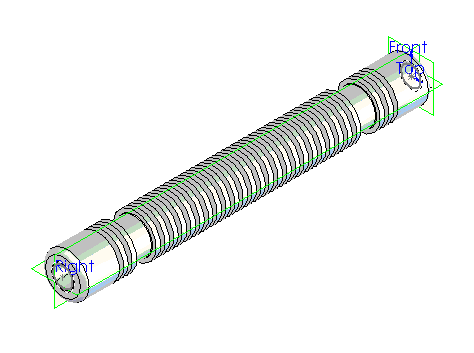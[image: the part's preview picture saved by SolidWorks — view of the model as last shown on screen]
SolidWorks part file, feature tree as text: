
SOLIDWORKS PART (.sldprt)
format: sldprt  version: not decoded by parser v0  size: 542,720 bytes
history: native  units: mm
features: sketch x9, hole x2, thread x2, extrude x1, cut_extrude x1, cut_revolve x1, fillet x1 (+11 scaffold rows collapsed)
feature tree (28):
  scaffold x11  (default folders/planes/origin — collapsed)
  sketch  "Sketch1"  dims[D1=31.75mm]
  extrude  "Extrude1"  Depth=254mm
  sketch  "Sketch2"  dims[D1=6.35mm]
  cut_extrude  "Cut-Extrude1"  [1 undecoded]
  sketch  "Sketch6"  dims[D1=14.2875mm]
  sketch  "Sketch7"  dims[D1=14.2875mm]
  sketch  "Sketch8"  dims[c1.D3=0.381mm c1.D9=0.381mm c1.D1=12.7mm c1.D2=6.35mm c2.D3=3.175mm c2.D4=3.175mm c2.D5=3.175mm c3.D4=~13.49375mm c3.D5=3.175mm c3.D6=127.0mm c3.D1=3.175mm c3.D2=3.175mm c3.D3=7.9375mm c4.D4=1.5875mm c4.D5=12.7mm c4.D6=127.0mm c4.D7=9.525mm c4.D8=12.7mm c4.D9=~18.581211mm c4.D1=3.175mm c4.D2=3.175mm c5.D8=7.9375mm c5.D2=3.175mm]
  cut_revolve  "Cut-Revolve1"  Angle=360deg
  fillet  "Fillet1"  Radius=3.175mm
  hole  "3/8 NPT Tapped Hole1"  Diameter=14.2748mm Depth=17.37868mm
  sketch  "3DSketch1"
  sketch  "Sketch10"  dims[hole-wizard template sketch: 50 standard entries collapsed; hole parameters kept: c13.Tap Drill Dia.=14.2748mm c13.Tap Drill Depth=~17.37868mm c13.Thread Dia.=~15.926054mm c13.D4=~22.362017mm c13.Thread Angle=3.43deg c13.Thread Depth=~10.33018mm c13.D6=~25.48394mm c13.Drill Angle=118.0deg]
  thread  "Cosmetic Thread1"  Diameter=10.33018mm  [1 undecoded]
  hole  "3/8 NPT Tapped Hole2"  Diameter=14.2748mm Depth=17.37901mm
  sketch  "3DSketch2"
  sketch  "Sketch11"  dims[hole-wizard template sketch: 50 standard entries collapsed; hole parameters kept: c13.Tap Drill Dia.=14.2748mm c13.Tap Drill Depth=~17.37901mm c13.Thread Dia.=~15.926054mm c13.D4=~22.362017mm c13.Thread Angle=3.43deg c13.Thread Depth=~10.330002mm c13.D6=~25.48394mm c13.Drill Angle=118.0deg]
  thread  "Cosmetic Thread2"  Diameter=10.330002mm  [1 undecoded]
decode coverage: 14 of 17 modeling features carry decoded parameters
note: ~ marks probable driven/reference dimensions
note: 3 parameter values undecoded
note: suppression state not decoded; provenance and decode notes live in map.json
